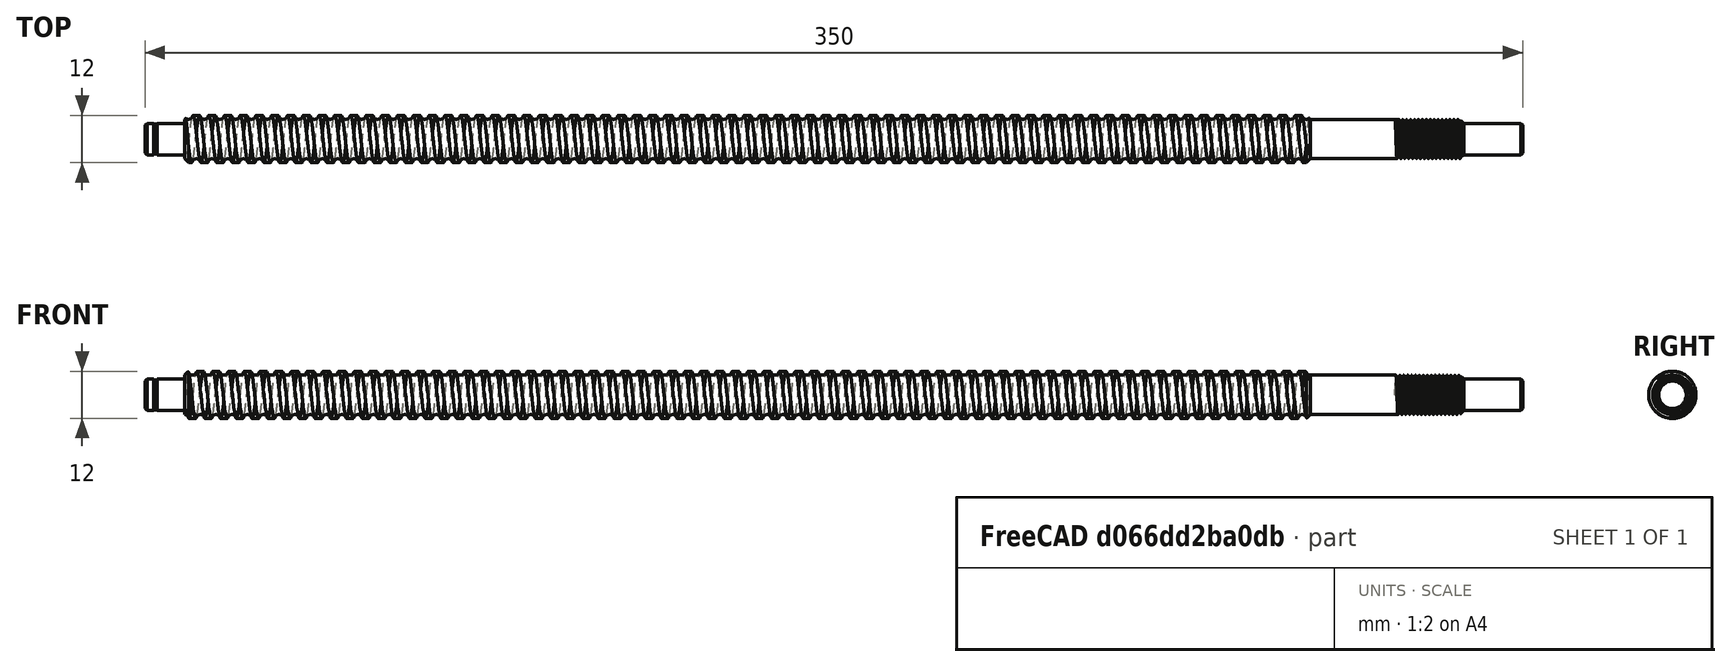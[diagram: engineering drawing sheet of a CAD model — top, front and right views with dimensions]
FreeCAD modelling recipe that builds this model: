
FCSTD DOCUMENT  (FreeCAD 0.15R4671 (Git))
Label: ballscrew-350
License: All rights reserved
LicenseURL: http://en.wikipedia.org/wiki/All_rights_reserved
objects: Sketcher::SketchObject×3, Part::Helix×2, Part::Sweep×2, Part::Cut×2, PartDesign::Revolution×1, PartDesign::Chamfer×1
note: 12 computed .brp shape members not serialized (recipe doc carries the construction recipe); baked Part::Feature solids carry a one-line shape summary decoded from their .brp

FEATURE [Sketcher::SketchObject] Sketch  label="base-sketch"
  Placement = pos=(0,0,0) rot=(1,0,0;1.5708rad)
  sketch-geometry (15):
    g0: LineSegment StartX=-153 StartY=0 StartZ=0 EndX=-153 EndY=4 EndZ=0
    g1: LineSegment StartX=-153 StartY=4 StartZ=0 EndX=-150.9 EndY=4 EndZ=0
    g2: LineSegment StartX=-150.9 StartY=4 StartZ=0 EndX=-150.9 EndY=3.8 EndZ=0
    g3: LineSegment StartX=-150.9 StartY=3.8 StartZ=0 EndX=-150 EndY=3.8 EndZ=0
    g4: LineSegment StartX=-150 StartY=3.8 StartZ=0 EndX=-150 EndY=4 EndZ=0
    g5: LineSegment StartX=-150 StartY=4 StartZ=0 EndX=-143 EndY=4 EndZ=0
    g6: LineSegment StartX=-143 StartY=4 StartZ=0 EndX=-143 EndY=5 EndZ=0
    g7: LineSegment StartX=-143 StartY=5 StartZ=0 EndX=-142 EndY=6 EndZ=0
    g8: LineSegment StartX=-142 StartY=6 StartZ=0 EndX=142 EndY=6 EndZ=0
    g9: LineSegment StartX=142 StartY=6 StartZ=0 EndX=143 EndY=5 EndZ=0
    g10: LineSegment StartX=143 StartY=5 StartZ=0 EndX=181 EndY=5 EndZ=0
    g11: LineSegment StartX=181 StartY=5 StartZ=0 EndX=182 EndY=4 EndZ=0
    g12: LineSegment StartX=182 StartY=4 StartZ=0 EndX=197 EndY=4 EndZ=0
    g13: LineSegment StartX=197 StartY=4 StartZ=0 EndX=197 EndY=0 EndZ=0
    g14: LineSegment StartX=197 StartY=0 StartZ=0 EndX=-153 EndY=0 EndZ=0
  constraints (45):
    c: PointOnObject(g0,g-1)
    c: Vertical(g0)
    c: Coincident(g0,g1)
    c: Horizontal(g1)
    c: Coincident(g1,g2)
    c: Coincident(g2,g3)
    c: Horizontal(g3)
    c: Coincident(g3,g4)
    c: Vertical(g4)
    c: Coincident(g4,g5)
    c: Horizontal(g5)
    c: Coincident(g5,g6)
    c: Coincident(g6,g7)
    c: Coincident(g7,g8)
    c: Horizontal(g8)
    c: Coincident(g8,g9)
    c: Coincident(g9,g10)
    c: Horizontal(g10)
    c: Coincident(g10,g11)
    c: Coincident(g11,g12)
    c: Horizontal(g12)
    c: Coincident(g12,g13)
    c: PointOnObject(g13,g-1)
    c: Vertical(g13)
    c: Coincident(g13,g14)
    c: Coincident(g14,g0)
    c: Vertical(g2)
    c: PointOnObject(g4,g1)
    c: DistanceY(g0,g0) = -4
    c: DistanceY(g1,g2) = -0.2
    c: DistanceX(g2,g3) = 0.9
    c: Vertical(g6)
    c: Angle(g6,g7) = 2.35619
    c: DistanceX(g5,g0) = -10
    c: DistanceX(g3,g5) = 7
    c: DistanceY(g7,g0) = -6
    c: DistanceY(g9,g13) = -5
    c: Angle(g8,g9) = 2.35619
    c: Angle(g10,g11) = 2.35619
    c: DistanceY(g6,g0) = -5
    c: DistanceX(g13,g11) = -15
    c: DistanceY(g12,g13) = -4
    c: DistanceX(g11,g9) = -39
    c: DistanceX(g13,g0) = -350
    c: Symmetric(g9,g6,g-2)
FEATURE [PartDesign::Revolution] Revolution  label="base"
  Angle = 360
  Axis = (1,0,0)
  Base = (0,0,0)
  Placement = pos=(0,0,0) rot=(1,0,0;1.5708rad)
  ReferenceAxis = -> Sketch [H_Axis]
  Sketch = -> Sketch
FEATURE [Part::Helix] Helix001  label="thread-neg-helix"
  Angle = 0
  Height = 300
  LocalCoord = 0
  Pitch = 4
  Placement = pos=(-150,0,0) rot=(0.57735,0.57735,0.57735;2.0944rad)
  Radius = 6.2
  Style = 1
FEATURE [Sketcher::SketchObject] Sketch001  label="thread-neg-sketch"
  sketch-geometry (1):
    g0: Circle CenterX=-150 CenterY=6.2 CenterZ=0 NormalX=0 NormalY=0 NormalZ=1 Radius=1.19
  constraints (3):
    c: DistanceX(g-1,g0) = -150
    c: DistanceY(g-1,g0) = 6.2
    c: Radius(g0) = 1.19
FEATURE [Part::Sweep] Sweep  label="thread-neg"
  Frenet = true
  Sections = -> [Sketch001]
  Solid = true
  Spine = -> Helix001 [Edge1,Edge2,Edge3,Edge4,Edge5,Edge6,Edge7,Edge8,Edge9,Edge10,Edge11,Edge12,Edge13,Edge14,Edge15,Edge16,Edge17,Edge18,Edge19,Edge20,Edge21,Edge22,Edge23,Edge24,Edge25,Edge26,Edge27,Edge28,Edge29,Edge30,Edge31,Edge32,Edge33,Edge34,Edge35,Edge36,Edge37,Edge38,Edge39,Edge40,+35 more]
  Transition = 1
FEATURE [Part::Cut] Cut  label="threaded-rod"
  Base = -> Revolution
  Tool = -> Sweep
FEATURE [PartDesign::Chamfer] Chamfer  label="threaded-rod-chamfer"
  Base = -> Cut [Edge384,Edge1]
  Size = 0.5
FEATURE [Part::Helix] Helix  label="fix-thread-neg-helix"
  Angle = 0
  Height = 18
  LocalCoord = 0
  Pitch = 1
  Placement = pos=(165,0,0) rot=(0.57735,0.57735,0.57735;2.0944rad)
  Radius = 4.13
  Style = 1
FEATURE [Sketcher::SketchObject] Sketch002  label="fix-thread-neg-sketch"
  sketch-geometry (9):
    g0: LineSegment StartX=164.505 StartY=5.02737 StartZ=0 EndX=164.882 EndY=4.37487 EndZ=0
    g1: LineSegment StartX=165.118 StartY=4.37487 StartZ=0 EndX=165.495 EndY=5.02737 EndZ=0
    g2: LineSegment [constr] StartX=164.505 StartY=5.02737 StartZ=0 EndX=165.495 EndY=5.02737 EndZ=0
    g3: LineSegment StartX=164.505 StartY=5.02737 StartZ=0 EndX=164.505 EndY=5.12737 EndZ=0
    g4: LineSegment StartX=164.505 StartY=5.12737 StartZ=0 EndX=165.495 EndY=5.12737 EndZ=0
    g5: LineSegment StartX=165.495 StartY=5.02737 StartZ=0 EndX=165.495 EndY=5.12737 EndZ=0
    g6: LineSegment StartX=164.882 StartY=4.37487 StartZ=0 EndX=165.118 EndY=4.37487 EndZ=0
    g7: LineSegment [constr] StartX=164.882 StartY=4.37487 StartZ=0 EndX=165 EndY=4.17 EndZ=0
    g8: LineSegment [constr] StartX=165 StartY=4.17 StartZ=0 EndX=165.118 EndY=4.37487 EndZ=0
  constraints (25):
    c: Angle(g1,g0) = 1.0472
    c: Coincident(g2,g0)
    c: Horizontal(g2)
    c: Coincident(g1,g2)
    c: Equal(g1,g0)
    c: Coincident(g0,g3)
    c: Vertical(g3)
    c: Coincident(g3,g4)
    c: Horizontal(g4)
    c: Coincident(g5,g4)
    c: Vertical(g5)
    c: Coincident(g5,g1)
    c: DistanceY(g4,g1) = -0.1
    c: Horizontal(g6)
    c: Coincident(g0,g6)
    c: Coincident(g1,g6)
    c: DistanceX(g3,g4) = 0.99
    c: Coincident(g7,g8)
    c: Coincident(g8,g1)
    c: Angle(g8,g1) = 3.14159
    c: Coincident(g7,g0)
    c: Angle(g0,g7) = 3.14159
    c: DistanceX(g-1,g7) = 165
    c: DistanceY(g-1,g7) = 4.17
    c: DistanceY(g0,g0) = 0.6525
FEATURE [Part::Sweep] Sweep001  label="fix-thread-neg"
  Frenet = true
  Sections = -> [Sketch002]
  Solid = true
  Spine = -> Helix [Edge1,Edge2,Edge3,Edge4,Edge5,Edge6,Edge7,Edge8,Edge9,Edge10,Edge11,Edge12,Edge13,Edge14,Edge15,Edge16,Edge17,Edge18]
  Transition = 1
FEATURE [Part::Cut] Cut001  label="ballscrew-350"
  Base = -> Chamfer
  Tool = -> Sweep001
